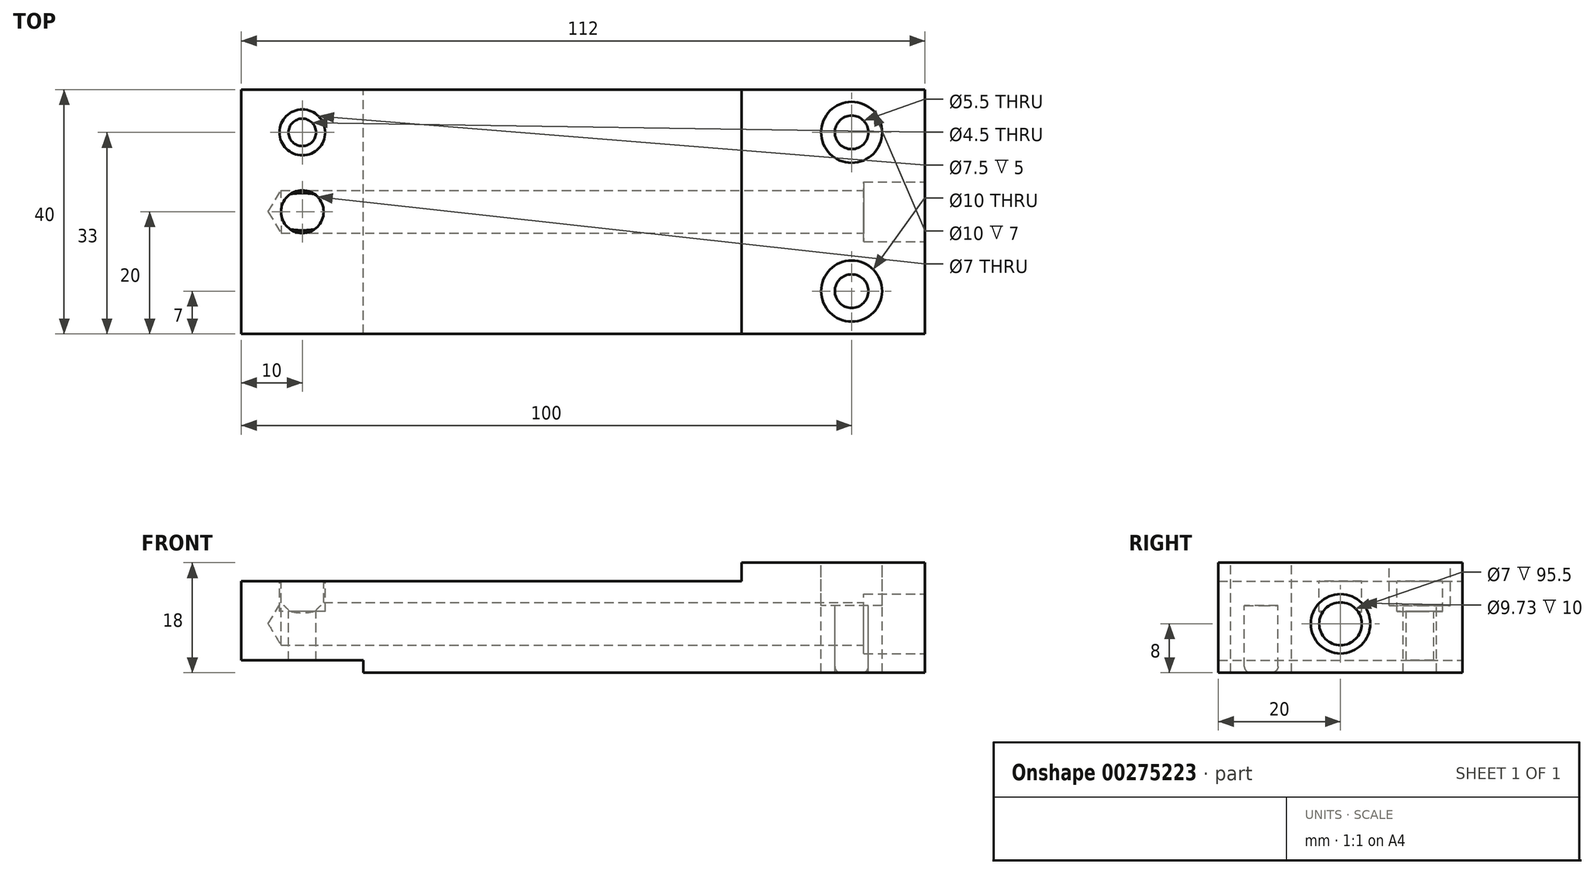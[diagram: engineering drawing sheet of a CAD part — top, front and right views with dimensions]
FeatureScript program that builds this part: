
annotation { "Feature Type Name" : "Feature", "Feature Type Description" : "" }
export const myFeature = defineFeature(function(context is Context, id is Id, definition is map)
    precondition{}
    {
        {
            var Q0;
            Q0=qCreatedBy(makeId("Front.planeOp"),FACE);
            var sketch = newSketch(context, id + "F0", { "sketchPlane" : qUnion([Q0])});
            skLineSegment(sketch, "E0", {"start": v(0, 0) * mm, "end": v(20, 0) * mm});
            skLineSegment(sketch, "E1", {"start": v(20, 0) * mm, "end": v(20, -2) * mm});
            skLineSegment(sketch, "E2", {"start": v(20, -2) * mm, "end": v(112, -2) * mm});
            skLineSegment(sketch, "E3", {"start": v(112, -2) * mm, "end": v(112, 16) * mm});
            skLineSegment(sketch, "E4", {"start": v(112, 16) * mm, "end": v(82, 16) * mm});
            skLineSegment(sketch, "E5", {"start": v(82, 16) * mm, "end": v(82, 13) * mm});
            skLineSegment(sketch, "E6", {"start": v(82, 13) * mm, "end": v(0, 13) * mm});
            skLineSegment(sketch, "E7", {"start": v(0, 13) * mm, "end": v(0, 0) * mm});
            skSolve(sketch);
        }
        {
            var Q0;
            Q0=makeQuery(id+"F0.imprint","IMPRINT",FACE,{"disambiguationData":[TD([[makeQuery(id+"F0.imprint","IMPRINT",EDGE,{"derivedFrom":sQuery(id+"F0.wireOp",EDGE,"E0")}),1.0]])]});
            extrude(context, id + "F1", {"entities" : qUnion([Q0]), "endBound" : BoundingType.SYMMETRIC, "depth" : 40 * mm});
        }
        {
            var Q0;
            Q0=makeQuery(id+"F1.opExtrude","SWEPT_FACE",FACE,{"disambiguationData":[OSD([sQuery(id+"F0.wireOp",EDGE,"E6")])]});
            var sketch = newSketch(context, id + "F2", { "sketchPlane" : qUnion([Q0])});
            skCircle(sketch, "E8", {"center": v(10, 13) * mm, "radius": 3.75 * mm});
            skCircle(sketch, "E9", {"center": v(10, 13) * mm, "radius": 2.25 * mm});
            skCircle(sketch, "E10.MirrorC", {"center": v(10, -13) * mm, "radius": 3.75 * mm});
            skCircle(sketch, "E11.MirrorC", {"center": v(10, -13) * mm, "radius": 2.25 * mm});
            skSolve(sketch);
        }
        {
            var Q0;
            Q0=makeQuery(id+"F2.imprint","IMPRINT",FACE,{"disambiguationData":[TD([[makeQuery(id+"F2.imprint","IMPRINT",EDGE,{"derivedFrom":sQuery(id+"F2.wireOp",EDGE,"E9")}),1.0]])]});
            extrude(context, id + "F3", {"entities" : qUnion([Q0]), "operationType" : NewBodyOperationType.REMOVE, "oppositeDirection" : true, "depth" : 25 * mm});
        }
        {
            var Q0;
            Q0=makeQuery(id+"F2.imprint","IMPRINT",FACE,{"disambiguationData":[TD([[makeQuery(id+"F2.imprint","IMPRINT",EDGE,{"derivedFrom":sQuery(id+"F2.wireOp",EDGE,"E8")}),1.0]])]});
            extrude(context, id + "F4", {"entities" : qUnion([Q0]), "operationType" : NewBodyOperationType.REMOVE, "oppositeDirection" : true, "depth" : 5 * mm});
        }
        {
            var Q0;
            Q0=makeQuery(id+"F1.opExtrude","SWEPT_FACE",FACE,{"disambiguationData":[OSD([sQuery(id+"F0.wireOp",EDGE,"E4")])]});
            var sketch = newSketch(context, id + "F5", { "sketchPlane" : qUnion([Q0])});
            skCircle(sketch, "E12", {"center": v(100, 13) * mm, "radius": 5 * mm});
            skCircle(sketch, "E13", {"center": v(100, 13) * mm, "radius": 2.75 * mm});
            skCircle(sketch, "E14.MirrorC", {"center": v(100, -13) * mm, "radius": 2.75 * mm});
            skCircle(sketch, "E15.MirrorC", {"center": v(100, -13) * mm, "radius": 5 * mm});
            skSolve(sketch);
        }
        {
            var Q0;
            Q0=makeQuery(id+"F5.imprint","IMPRINT",FACE,{"disambiguationData":[TD([[makeQuery(id+"F5.imprint","IMPRINT",EDGE,{"derivedFrom":sQuery(id+"F5.wireOp",EDGE,"E13")}),1.0]])]});
            var Q1;
            Q1=makeQuery(id+"F5.imprint","IMPRINT",FACE,{"disambiguationData":[TD([[makeQuery(id+"F5.imprint","IMPRINT",EDGE,{"derivedFrom":sQuery(id+"F5.wireOp",EDGE,"E14.MirrorC")}),-1.0]])]});
            extrude(context, id + "F6", {"entities" : qUnion([Q0, Q1]), "operationType" : NewBodyOperationType.REMOVE, "oppositeDirection" : true, "depth" : 25 * mm});
        }
        {
            var Q0;
            Q0=makeQuery(id+"F5.imprint","IMPRINT",FACE,{"disambiguationData":[TD([[makeQuery(id+"F5.imprint","IMPRINT",EDGE,{"derivedFrom":sQuery(id+"F5.wireOp",EDGE,"E12")}),1.0]])]});
            var Q1;
            Q1=makeQuery(id+"F5.imprint","IMPRINT",FACE,{"disambiguationData":[TD([[makeQuery(id+"F5.imprint","IMPRINT",EDGE,{"derivedFrom":sQuery(id+"F5.wireOp",EDGE,"E14.MirrorC")}),1.0]])]});
            extrude(context, id + "F7", {"entities" : qUnion([Q0, Q1]), "operationType" : NewBodyOperationType.REMOVE, "oppositeDirection" : true, "depth" : 7 * mm});
        }
        {
            var Q0;
            Q0=makeQuery(id+"F1.opExtrude","SWEPT_FACE",FACE,{"disambiguationData":[OSD([sQuery(id+"F0.wireOp",EDGE,"E3")])]});
            var sketch = newSketch(context, id + "F8", { "sketchPlane" : qUnion([Q0])});
            skLineSegment(sketch, "E16.0.0", {"start": v(20, -2) * mm, "end": v(20, 16) * mm});
            skLineSegment(sketch, "E16.0.1", {"start": v(20, 16) * mm, "end": v(-20, 16) * mm});
            skLineSegment(sketch, "E16.0.2", {"start": v(-20, 16) * mm, "end": v(-20, -2) * mm});
            skPoint(sketch, "E17.centerSnap0", {"position": v(0, 16) * mm});
            skPoint(sketch, "E17.centerSnap1", {"position": v(20, 7) * mm});
            skPoint(sketch, "E18", {"position": v(0, 6) * mm});
            skSolve(sketch);
        }
        {
            var Q0;
            Q0=sQuery(id+"F8.wireOp",VERTEX,"E18");
            var Q1;
            Q1=makeQuery(id+"F1.opExtrude","SWEPT_BODY",BODY,{"disambiguationData":[OSD([sQuery(id+"F0.wireOp",EDGE,"E0"),sQuery(id+"F0.wireOp",EDGE,"E1"),sQuery(id+"F0.wireOp",EDGE,"E2"),sQuery(id+"F0.wireOp",EDGE,"E3"),sQuery(id+"F0.wireOp",EDGE,"E4"),sQuery(id+"F0.wireOp",EDGE,"E5"),sQuery(id+"F0.wireOp",EDGE,"E6"),sQuery(id+"F0.wireOp",EDGE,"E7")])]});
            hole(context, id + "F9", {"style" : HoleStyle.C_BORE, "endStyle" : HoleEndStyle.BLIND, "holeDiameter" : 7 * mm, "cBoreDiameter" : 9.73 * mm, "cBoreDepth" : 10 * mm, "holeDepth" : 105.5 * mm, "tappedDepth" : 12 * mm, "tapClearance" : 3, "locations" : qUnion([Q0]), "scope" : qUnion([Q1])});
        }
        {
            var Q0;
            Q0=makeQuery(id+"F1.opExtrude","SWEPT_FACE",FACE,{"disambiguationData":[OSD([sQuery(id+"F0.wireOp",EDGE,"E6")])]});
            var sketch = newSketch(context, id + "F10", { "sketchPlane" : qUnion([Q0])});
            skPoint(sketch, "E19", {"position": v(10, 0) * mm});
            skSolve(sketch);
        }
        {
            var Q0;
            Q0=sQuery(id+"F10.wireOp",VERTEX,"E19");
            var Q1;
            Q1=makeQuery(id+"F1.opExtrude","SWEPT_BODY",BODY,{"disambiguationData":[OSD([sQuery(id+"F0.wireOp",EDGE,"E0"),sQuery(id+"F0.wireOp",EDGE,"E1"),sQuery(id+"F0.wireOp",EDGE,"E2"),sQuery(id+"F0.wireOp",EDGE,"E3"),sQuery(id+"F0.wireOp",EDGE,"E4"),sQuery(id+"F0.wireOp",EDGE,"E5"),sQuery(id+"F0.wireOp",EDGE,"E6"),sQuery(id+"F0.wireOp",EDGE,"E7")])]});
            hole(context, id + "F11", {"style" : HoleStyle.SIMPLE, "endStyle" : HoleEndStyle.BLIND, "holeDiameter" : 7 * mm, "holeDepth" : 5 * mm, "tappedDepth" : 12 * mm, "tapClearance" : 3, "locations" : qUnion([Q0]), "scope" : qUnion([Q1])});
        }
        {
            var Q0;
            Q0=makeQuery(id+"F1.opExtrude","CAP_EDGE",EDGE,{"disambiguationData":[OSD([sQuery(id+"F0.wireOp",EDGE,"E6")])],"isStart":false});
            var Q1;
            Q1=makeQuery(id+"F1.opExtrude","CAP_EDGE",EDGE,{"disambiguationData":[OSD([sQuery(id+"F0.wireOp",EDGE,"E6")])],"isStart":true});
            var Q2;
            Q2=makeQuery(id+"F1.opExtrude","SWEPT_EDGE",EDGE,{"disambiguationData":[OSD([sQuery(id+"F0.wireOp",EDGE,"E6"),sQuery(id+"F0.wireOp",EDGE,"E7")])]});
            var Q3;
            Q3=makeQuery(id+"F1.opExtrude","SWEPT_EDGE",EDGE,{"disambiguationData":[OSD([sQuery(id+"F0.wireOp",EDGE,"E5"),sQuery(id+"F0.wireOp",EDGE,"E6")])]});
            var Q4;
            Q4=makeQuery(id+"F1.opExtrude","SWEPT_EDGE",EDGE,{"disambiguationData":[OSD([sQuery(id+"F0.wireOp",EDGE,"E4"),sQuery(id+"F0.wireOp",EDGE,"E5")])]});
            var Q5;
            Q5=makeQuery(id+"F1.opExtrude","CAP_EDGE",EDGE,{"disambiguationData":[OSD([sQuery(id+"F0.wireOp",EDGE,"E4")])],"isStart":false});
            var Q6;
            Q6=makeQuery(id+"F1.opExtrude","CAP_EDGE",EDGE,{"disambiguationData":[OSD([sQuery(id+"F0.wireOp",EDGE,"E4")])],"isStart":true});
            var Q7;
            Q7=makeQuery(id+"F1.opExtrude","SWEPT_EDGE",EDGE,{"disambiguationData":[OSD([sQuery(id+"F0.wireOp",EDGE,"E3"),sQuery(id+"F0.wireOp",EDGE,"E4")])]});
            var Q8;
            Q8=makeQuery(id+"F1.opExtrude","CAP_FACE",FACE,{"disambiguationData":[OSD([sQuery(id+"F0.wireOp",EDGE,"E0"),sQuery(id+"F0.wireOp",EDGE,"E1"),sQuery(id+"F0.wireOp",EDGE,"E2"),sQuery(id+"F0.wireOp",EDGE,"E3"),sQuery(id+"F0.wireOp",EDGE,"E4"),sQuery(id+"F0.wireOp",EDGE,"E5"),sQuery(id+"F0.wireOp",EDGE,"E6"),sQuery(id+"F0.wireOp",EDGE,"E7")])],"isStart":false});
            var Q9;
            Q9=makeQuery(id+"F1.opExtrude","SWEPT_EDGE",EDGE,{"disambiguationData":[OSD([sQuery(id+"F0.wireOp",EDGE,"E0"),sQuery(id+"F0.wireOp",EDGE,"E7")])]});
            var Q10;
            Q10=makeQuery(id+"F1.opExtrude","CAP_EDGE",EDGE,{"disambiguationData":[OSD([sQuery(id+"F0.wireOp",EDGE,"E2")])],"isStart":true});
            var Q11;
            Q11=makeQuery(id+"F1.opExtrude","CAP_EDGE",EDGE,{"disambiguationData":[OSD([sQuery(id+"F0.wireOp",EDGE,"E7")])],"isStart":true});
            var Q12;
            Q12=makeQuery(id+"F1.opExtrude","CAP_EDGE",EDGE,{"disambiguationData":[OSD([sQuery(id+"F0.wireOp",EDGE,"E0")])],"isStart":true});
            var Q13;
            Q13=makeQuery(id+"F1.opExtrude","CAP_EDGE",EDGE,{"disambiguationData":[OSD([sQuery(id+"F0.wireOp",EDGE,"E1")])],"isStart":true});
            var Q14;
            Q14=makeQuery(id+"F4.boolean.opBoolean","COPY",EDGE,{"derivedFrom":makeQuery(id+"F4.opExtrude","CAP_EDGE",EDGE,{"disambiguationData":[OSD([sQuery(id+"F2.wireOp",EDGE,"E8")])],"isStart":true})});
            var Q15;
            Q15=makeQuery(id+"F11.hole-0.boolean.opBoolean","COPY",EDGE,{"derivedFrom":makeQuery(id+"F11.hole-0.opRevolve","SWEPT_EDGE",EDGE,{"disambiguationData":[OSD([sQuery(id+"F11.hole-0.sketch.wireOp",EDGE,"core_line_2"),sQuery(id+"F11.hole-0.sketch.wireOp",EDGE,"core_line_3")])]})});
            var Q16;
            Q16=makeQuery(id+"F2sbiF5R3TB2QD5_1.1.F4.boolean.opBoolean","COPY",EDGE,{"derivedFrom":makeQuery(id+"F2sbiF5R3TB2QD5_1.1.F4.opExtrude","CAP_EDGE",EDGE,{"disambiguationData":[OSD([sQuery(id+"F2.wireOp",EDGE,"E8")])],"isStart":true})});
            var Q17;
            Q17=makeQuery(id+"F7.boolean.opBoolean","COPY",EDGE,{"derivedFrom":makeQuery(id+"F7.opExtrude","CAP_EDGE",EDGE,{"disambiguationData":[OSD([sQuery(id+"F5.wireOp",EDGE,"E12")])],"isStart":true})});
            var Q18;
            Q18=makeQuery(id+"F7.boolean.opBoolean","COPY",EDGE,{"derivedFrom":makeQuery(id+"F7.opExtrude","CAP_EDGE",EDGE,{"disambiguationData":[OSD([sQuery(id+"F5.wireOp",EDGE,"E15.MirrorC")])],"isStart":true})});
            var Q19;
            Q19=makeQuery(id+"F1.opExtrude","CAP_EDGE",EDGE,{"disambiguationData":[OSD([sQuery(id+"F0.wireOp",EDGE,"E3")])],"isStart":true});
            var Q20;
            Q20=makeQuery(id+"F1.opExtrude","SWEPT_EDGE",EDGE,{"disambiguationData":[OSD([sQuery(id+"F0.wireOp",EDGE,"E2"),sQuery(id+"F0.wireOp",EDGE,"E3")])]});
            var Q21;
            Q21=makeQuery(id+"F6.boolean.opBoolean","INTERSECT",EDGE,{"derivedFrom":[makeQuery(id+"F1.opExtrude","SWEPT_FACE",FACE,{"disambiguationData":[OSD([sQuery(id+"F0.wireOp",EDGE,"E2")])]}),makeQuery(id+"F6.opExtrude","SWEPT_FACE",FACE,{"disambiguationData":[OSD([sQuery(id+"F5.wireOp",EDGE,"E14.MirrorC")])]})]});
            var Q22;
            Q22=makeQuery(id+"F6.boolean.opBoolean","INTERSECT",EDGE,{"derivedFrom":[makeQuery(id+"F1.opExtrude","SWEPT_FACE",FACE,{"disambiguationData":[OSD([sQuery(id+"F0.wireOp",EDGE,"E2")])]}),makeQuery(id+"F6.opExtrude","SWEPT_FACE",FACE,{"disambiguationData":[OSD([sQuery(id+"F5.wireOp",EDGE,"E13")])]})]});
            var Q23;
            Q23=makeQuery(id+"F3.boolean.opBoolean","INTERSECT",EDGE,{"derivedFrom":[makeQuery(id+"F1.opExtrude","SWEPT_FACE",FACE,{"disambiguationData":[OSD([sQuery(id+"F0.wireOp",EDGE,"E0")])]}),makeQuery(id+"F3.opExtrude","SWEPT_FACE",FACE,{"disambiguationData":[OSD([sQuery(id+"F2.wireOp",EDGE,"E9")])]})]});
            var Q24;
            Q24=makeQuery(id+"F2sbiF5R3TB2QD5_1.1.F3.boolean.opBoolean","INTERSECT",EDGE,{"derivedFrom":[makeQuery(id+"F1.opExtrude","SWEPT_FACE",FACE,{"disambiguationData":[OSD([sQuery(id+"F0.wireOp",EDGE,"E0")])]}),makeQuery(id+"F2sbiF5R3TB2QD5_1.1.F3.opExtrude","SWEPT_FACE",FACE,{"disambiguationData":[OSD([sQuery(id+"F2.wireOp",EDGE,"E9")])]})]});
            var Q25;
            Q25=makeQuery(id+"F1.opExtrude","SWEPT_EDGE",EDGE,{"disambiguationData":[OSD([sQuery(id+"F0.wireOp",EDGE,"E1"),sQuery(id+"F0.wireOp",EDGE,"E2")])]});
            var Q26;
            Q26=makeQuery(id+"F1.opExtrude","SWEPT_EDGE",EDGE,{"disambiguationData":[OSD([sQuery(id+"F0.wireOp",EDGE,"E0"),sQuery(id+"F0.wireOp",EDGE,"E1")])]});
            var Q27;
            Q27=makeQuery(id+"F9.hole-0.boolean.opBoolean","COPY",EDGE,{"derivedFrom":makeQuery(id+"F9.hole-0.opRevolve","SWEPT_EDGE",EDGE,{"disambiguationData":[OSD([sQuery(id+"F9.hole-0.sketch.wireOp",EDGE,"cbore_start_line_2"),sQuery(id+"F9.hole-0.sketch.wireOp",EDGE,"cbore_start_line_3")])]})});
            fillet(context, id + "F12", {"entities" : qUnion([Q0, Q1, Q2, Q3, Q4, Q5, Q6, Q7, Q8, Q9, Q10, Q11, Q12, Q13, Q14, Q15, Q16, Q17, Q18, Q19, Q20, Q21, Q22, Q23, Q24, Q25, Q26, Q27]), "radius" : 1 * mm, "tangentPropagation" : true, "allowEdgeOverflow" : false});
        }
    });
